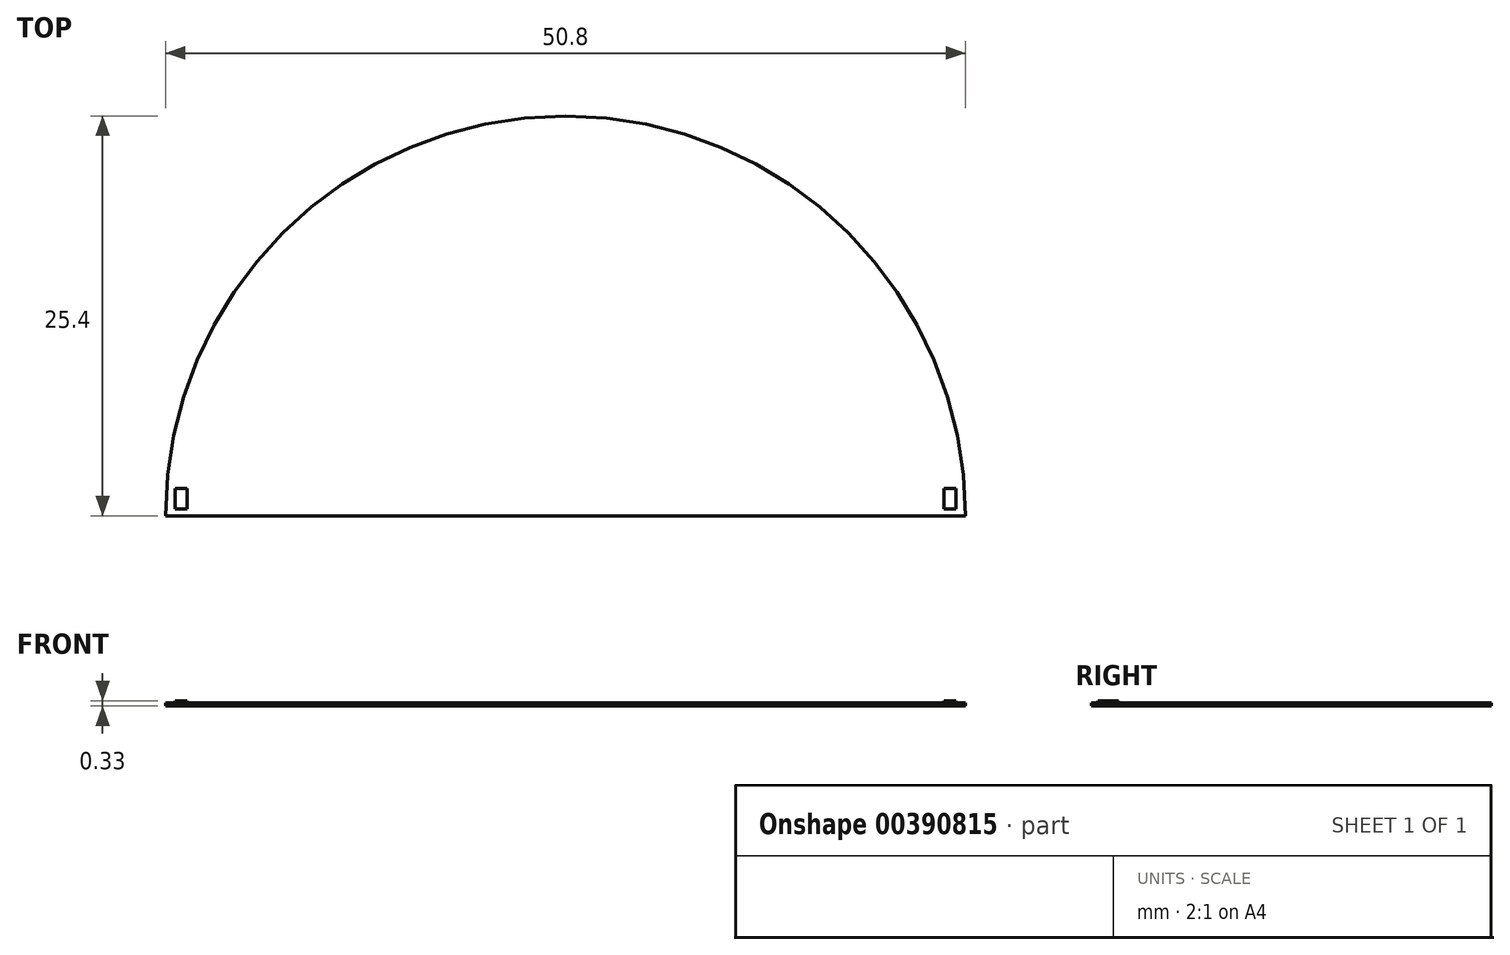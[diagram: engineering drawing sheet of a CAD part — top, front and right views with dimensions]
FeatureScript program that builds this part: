
annotation { "Feature Type Name" : "Feature", "Feature Type Description" : "" }
export const myFeature = defineFeature(function(context is Context, id is Id, definition is map)
    precondition{}
    {
        {
            var Q0;
            Q0=qCreatedBy(makeId("Top.planeOp"),FACE);
            var sketch = newSketch(context, id + "F0", { "sketchPlane" : qUnion([Q0])});
            skLineSegment(sketch, "E0", {"start": v(-25.4, -6.3) * mm, "end": v(25.4, -6.3) * mm});
            skArc(sketch, "E1", {"start": v(25.4, -6.3) * mm, "mid": v(0, 19.1) * mm, "end": v(-25.4, -6.3) * mm});
            skLineSegment(sketch, "E2", {"start": v(0, 50.83) * mm, "end": v(0, -55.92) * mm, "construction": true});
            skLineSegment(sketch, "E3.bottom", {"start": v(-24.8, -4.58) * mm, "end": v(-24.04, -4.58) * mm});
            skLineSegment(sketch, "E3.top", {"start": v(-24.8, -5.87) * mm, "end": v(-24.04, -5.87) * mm});
            skLineSegment(sketch, "E3.left", {"start": v(-24.8, -4.58) * mm, "end": v(-24.8, -5.87) * mm});
            skLineSegment(sketch, "E3.right", {"start": v(-24.04, -4.58) * mm, "end": v(-24.04, -5.87) * mm});
            skLineSegment(sketch, "E4.MirrorCS", {"start": v(24.04, -4.58) * mm, "end": v(24.04, -5.87) * mm});
            skLineSegment(sketch, "E5.MirrorCS", {"start": v(24.8, -4.58) * mm, "end": v(24.8, -5.87) * mm});
            skLineSegment(sketch, "E6.MirrorCS", {"start": v(24.8, -4.58) * mm, "end": v(24.04, -4.58) * mm});
            skLineSegment(sketch, "E7.MirrorCS", {"start": v(24.8, -5.87) * mm, "end": v(24.04, -5.87) * mm});
            skSolve(sketch);
        }
        {
            var Q0;
            Q0=makeQuery(id+"F0.imprint","IMPRINT",FACE,{"disambiguationData":[TD([[makeQuery(id+"F0.imprint","IMPRINT",EDGE,{"derivedFrom":sQuery(id+"F0.wireOp",EDGE,"E0")}),1.0]])]});
            var Q1;
            Q1=makeQuery(id+"F0.imprint","IMPRINT",FACE,{"disambiguationData":[TD([[makeQuery(id+"F0.imprint","IMPRINT",EDGE,{"derivedFrom":sQuery(id+"F0.wireOp",EDGE,"E3.bottom")}),-1.0]])]});
            var Q2;
            Q2=makeQuery(id+"F0.imprint","IMPRINT",FACE,{"disambiguationData":[TD([[makeQuery(id+"F0.imprint","IMPRINT",EDGE,{"derivedFrom":sQuery(id+"F0.wireOp",EDGE,"E4.MirrorCS")}),1.0]])]});
            extrude(context, id + "F1", {"entities" : qUnion([Q0, Q1, Q2]), "oppositeDirection" : true, "depth" : 0.2 * mm});
        }
        {
            var Q0;
            Q0=makeQuery(id+"F0.imprint","IMPRINT",FACE,{"disambiguationData":[TD([[makeQuery(id+"F0.imprint","IMPRINT",EDGE,{"derivedFrom":sQuery(id+"F0.wireOp",EDGE,"E3.bottom")}),-1.0]])]});
            var Q1;
            Q1=makeQuery(id+"F0.imprint","IMPRINT",FACE,{"disambiguationData":[TD([[makeQuery(id+"F0.imprint","IMPRINT",EDGE,{"derivedFrom":sQuery(id+"F0.wireOp",EDGE,"E4.MirrorCS")}),1.0]])]});
            extrude(context, id + "F2", {"entities" : qUnion([Q0, Q1]), "operationType" : NewBodyOperationType.ADD, "depth" : 0.13 * mm});
        }
    });
